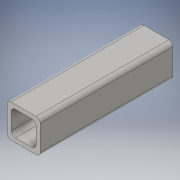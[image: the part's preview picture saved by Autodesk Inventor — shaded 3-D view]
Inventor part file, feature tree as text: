
AUTODESK INVENTOR PART (.ipt)
format: ipt  version: 2016 (Build 200138000, 138)  size: 113,152 bytes
history: native  units: in
note: dims shown in document units (in); Inventor stores cm internally (conversion verified against a paired STEP export)
features: extrude x1, sketch x1
ambient origin geometry x8: Origin, YZ Plane, XZ Plane, XY Plane, X Axis, Y Axis, Z Axis, Center Point
bodies: Solid1 (feature_tree)
feature tree (2):
  extrude  "Extrusion1"  Depth=1.0in
  sketch  "Sketch1"  dims[d0=1.0in d1=1.0in d2=0.125in d3=0.125in d4=4.0in d5=0.0in]
